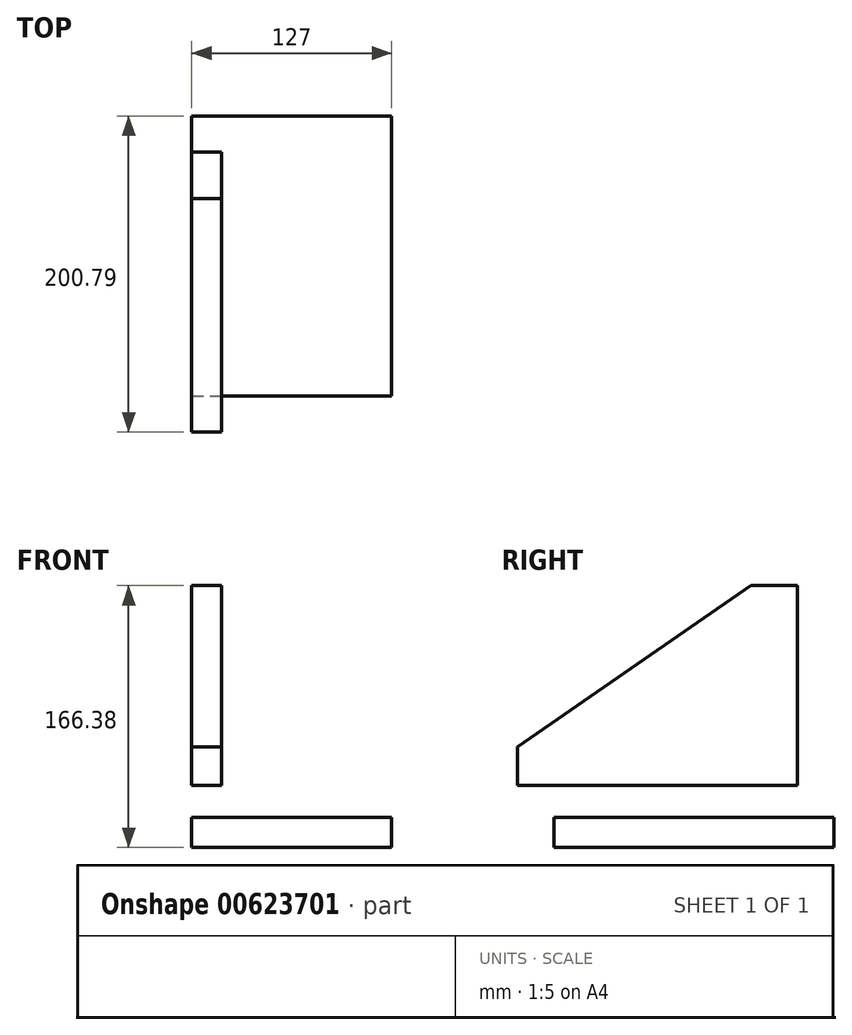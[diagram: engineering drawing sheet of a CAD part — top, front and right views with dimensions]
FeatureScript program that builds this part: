
annotation { "Feature Type Name" : "Feature", "Feature Type Description" : "" }
export const myFeature = defineFeature(function(context is Context, id is Id, definition is map)
    precondition{}
    {
        {
            var Q0;
            Q0=qCreatedBy(makeId("Top.planeOp"),FACE);
            var sketch = newSketch(context, id + "F0", { "sketchPlane" : qUnion([Q0])});
            skLineSegment(sketch, "E0.bottom", {"start": v(0, 0) * mm, "end": v(127, 0) * mm});
            skLineSegment(sketch, "E0.top", {"start": v(0, 177.8) * mm, "end": v(127, 177.8) * mm});
            skLineSegment(sketch, "E0.left", {"start": v(0, 0) * mm, "end": v(0, 177.8) * mm});
            skLineSegment(sketch, "E0.right", {"start": v(127, 0) * mm, "end": v(127, 177.8) * mm});
            skSolve(sketch);
        }
        {
            var Q0;
            Q0=makeQuery(id+"F0.imprint","IMPRINT",FACE,{"disambiguationData":[TD([[makeQuery(id+"F0.imprint","IMPRINT",EDGE,{"derivedFrom":sQuery(id+"F0.wireOp",EDGE,"E0.bottom")}),1.0]])]});
            extrude(context, id + "F1", {"entities" : qUnion([Q0]), "depth" : 19.05 * mm, "offsetDistance" : 25.4 * mm});
        }
        {
            var Q0;
            Q0=qCreatedBy(makeId("Right.planeOp"),FACE);
            var sketch = newSketch(context, id + "F2", { "sketchPlane" : qUnion([Q0])});
            skLineSegment(sketch, "E1.bottom", {"start": v(-23, 39.38) * mm, "end": v(154.8, 39.38) * mm});
            skLineSegment(sketch, "E1.top", {"start": v(-23, 166.38) * mm, "end": v(154.8, 166.38) * mm});
            skLineSegment(sketch, "E1.left", {"start": v(-23, 39.38) * mm, "end": v(-23, 166.38) * mm});
            skLineSegment(sketch, "E1.right", {"start": v(154.8, 39.38) * mm, "end": v(154.8, 166.38) * mm});
            skSolve(sketch);
        }
        {
            var Q0;
            Q0=makeQuery(id+"F2.imprint","IMPRINT",FACE,{"disambiguationData":[TD([[makeQuery(id+"F2.imprint","IMPRINT",EDGE,{"derivedFrom":sQuery(id+"F2.wireOp",EDGE,"E1.bottom")}),1.0]])]});
            extrude(context, id + "F3", {"entities" : qUnion([Q0]), "depth" : 19.05 * mm, "offsetDistance" : 25.4 * mm});
        }
        {
            var Q0;
            Q0=makeQuery(id+"F3.opExtrude","CAP_FACE",FACE,{"disambiguationData":[OSD([sQuery(id+"F2.wireOp",EDGE,"E1.bottom"),sQuery(id+"F2.wireOp",EDGE,"E1.top"),sQuery(id+"F2.wireOp",EDGE,"E1.left"),sQuery(id+"F2.wireOp",EDGE,"E1.right")])],"isStart":false});
            var sketch = newSketch(context, id + "F4", { "sketchPlane" : qUnion([Q0])});
            skLineSegment(sketch, "E2", {"start": v(125.3, 166.38) * mm, "end": v(-23, 63.82) * mm});
            skSolve(sketch);
        }
        {
            var Q0;
            Q0 = qSketchRegion(id + "F4", true);
            var Q1;
            {var subQ0=sQuery(id+"F4.wireOp",EDGE,"E2");Q1=makeQuery(id+"F4.imprint","IMPRINT",FACE,{"disambiguationData":[TD([[makeQuery(id+"F4.imprint","IMPRINT",EDGE,{"derivedFrom":subQ0}),-1.0]])]});}
            var Q2;
            Q2=makeQuery(id+"F3.opExtrude","CAP_FACE",FACE,{"disambiguationData":[OSD([sQuery(id+"F2.wireOp",EDGE,"E1.bottom"),sQuery(id+"F2.wireOp",EDGE,"E1.top"),sQuery(id+"F2.wireOp",EDGE,"E1.left"),sQuery(id+"F2.wireOp",EDGE,"E1.right")])],"isStart":true});
            extrude(context, id + "F5", {"entities" : qUnion([Q0, Q1, Q2]), "operationType" : NewBodyOperationType.REMOVE, "oppositeDirection" : true, "depth" : 25.4 * mm, "offsetDistance" : 25.4 * mm});
        }
    });
